# Revit family: Doors_Swing_Avanti_Systems_Pivot-Frameless-Pair-Swing-Door-Sgl-Glazed
name_source: partatom
category: Doors
revit_build: Autodesk Revit Architecture 2015 (Build: 20140606_1530(x64)
units: mm (PartAtom-declared; Revit-internal decimal feet)

## types (1)
- Load Family Type Catalog
    Acoustic performance (dB) = 43
    Analytic Construction = <None>
    BIMobject category = Swing
    BIMobject category code = doors-swing
    BIMobject main category = Doors
    BIMobject main category code = doors
    Brand url = http://www.avantisystemsusa.com
    Clear Anodic Finish = available
    Description = The Pivot Frameless Glass Swing Door is our luxury glass door solution that is completely customizable and is compatible with every partition system we offer as well as solid traditional walls.
    Design country = United States
    Edition number = 1
    Function = Interior
    Glass Marker = Yes
    Glass Material = Glass - Avanti -  Clear Tempered
    Glazing = Safety Glazing SGCC
    IFC Classification = Door
    LEED compatibility = YES
    Lock = Thumb turn floor lock with a key
    Manufacturer = Avanti Systems USA
    Manufacturer name = Avanti Systems
    Masterformat 2014 Code = 08 14 00
    Masterformat 2014 Description = Wood Doors
    Material main = Glass
    Material secondary = Aluminium
    Model = Pivot Frameless Swing Door
    Nominal height = 0"
    Nominal width = 0"
    OmniClass Code = 23-17 11 15
    OmniClass Description = Wood Doors
    Power = 110 V
    Product Guid = 3a11851e-372f-40ff-a97e-0ea9b5931639
    Product SKU = avanti-pivot-frameless-swing-door
    Product data url = https://bimobject.com
    Product family = Pivot & Hinged Doors
    Product group = Pivot Frameless Swing
    Product url = https://www.avantisystemsusa.com
    QR code = http://bimobject.com
    Sound Rating = 0
    Thickness = 1"
    Type = 2
    UNSPSC Code = 30171504
    URL = https://www.avantisystemsusa.com
    Uniclass 1.4 Code = JL20
    Uniclass 1.4 Description = Doors
    Uniclass 2015 Code = EF_25_30
    Uniclass 2015 Name = Doors and windows
    Uniformat II Code = C1020
    Uniformat II Description = Interior Doors
    Warranty = 1 year
    Weight Net (Kg) = 0

## geometry (parser evidence)
native form markers: Sweep x36
no freeform markers — native parametric forms only
